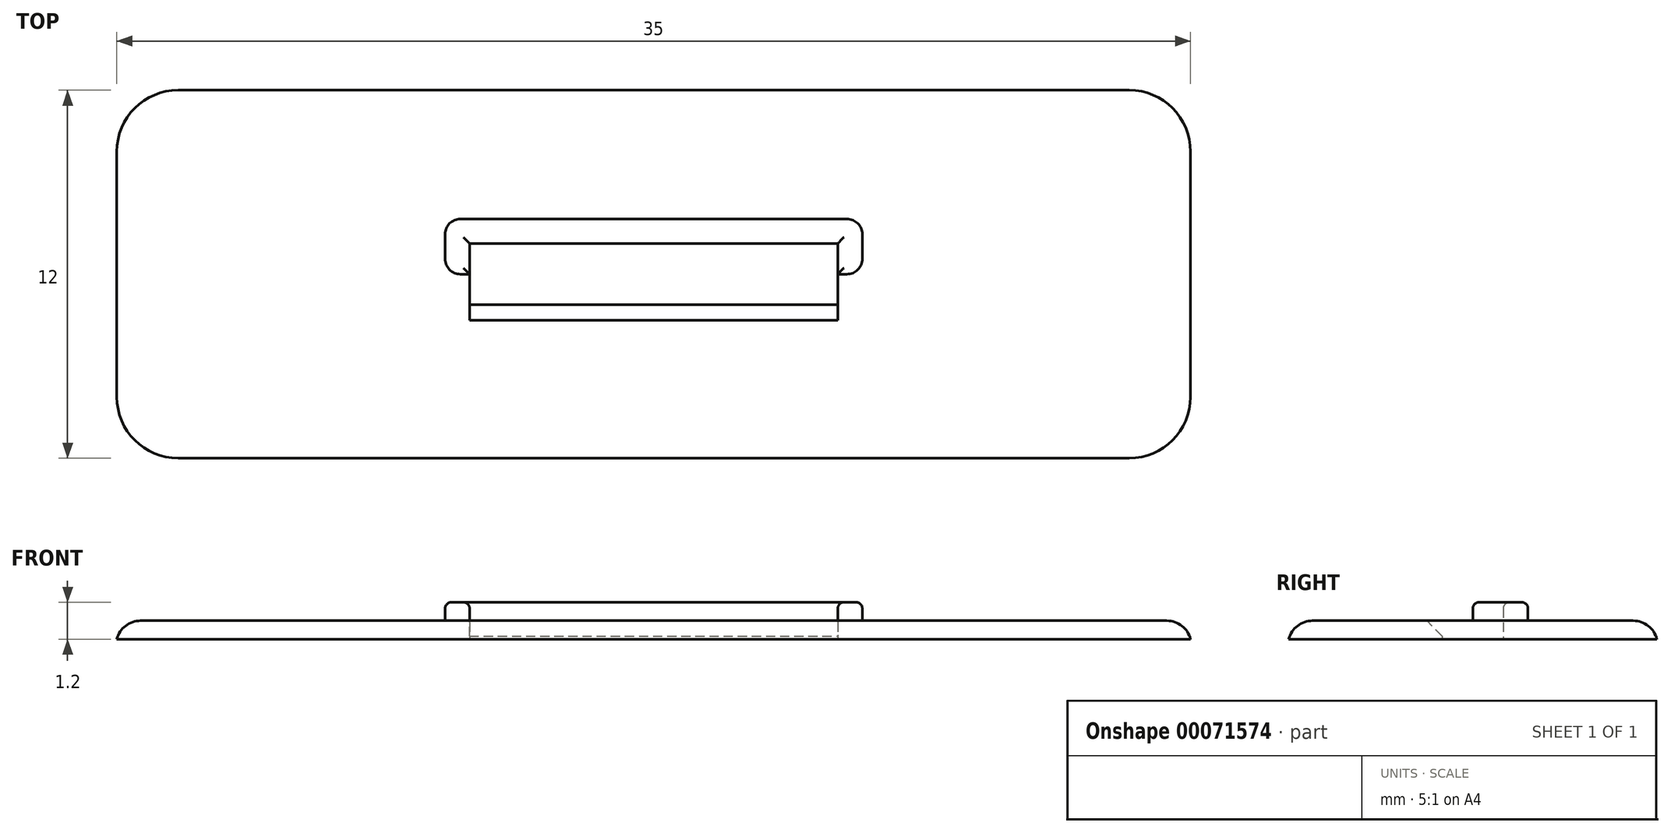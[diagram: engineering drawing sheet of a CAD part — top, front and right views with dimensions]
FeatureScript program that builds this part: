
annotation { "Feature Type Name" : "Feature", "Feature Type Description" : "" }
export const myFeature = defineFeature(function(context is Context, id is Id, definition is map)
    precondition{}
    {
        {
            var Q0;
            Q0=qCreatedBy(makeId("Top.planeOp"),FACE);
            var sketch = newSketch(context, id + "F0", { "sketchPlane" : qUnion([Q0])});
            skLineSegment(sketch, "E0.rect.bottom", {"start": v(17.5, -6) * mm, "end": v(-17.5, -6) * mm});
            skLineSegment(sketch, "E0.rect.top", {"start": v(17.5, 6) * mm, "end": v(-17.5, 6) * mm});
            skLineSegment(sketch, "E0.rect.left", {"start": v(17.5, -6) * mm, "end": v(17.5, 6) * mm});
            skLineSegment(sketch, "E0.rect.right", {"start": v(-17.5, -6) * mm, "end": v(-17.5, 6) * mm});
            skPoint(sketch, "E0.rect.middle", {"position": v(0, 0) * mm});
            skLineSegment(sketch, "E1.bottom", {"start": v(-6, 1) * mm, "end": v(6, 1) * mm});
            skLineSegment(sketch, "E1.top", {"start": v(-6, -1) * mm, "end": v(6, -1) * mm});
            skLineSegment(sketch, "E1.left", {"start": v(-6, 1) * mm, "end": v(-6, -1) * mm});
            skLineSegment(sketch, "E1.right", {"start": v(6, 1) * mm, "end": v(6, -1) * mm});
            skPoint(sketch, "E2", {"position": v(0, 1) * mm});
            skPoint(sketch, "E3", {"position": v(6, 0) * mm});
            skSolve(sketch);
        }
        {
            var Q0;
            Q0=qSketchRegion(id+"F0",true);
            extrude(context, id + "F1", {"entities" : qUnion([Q0]), "depth" : 0.6 * mm});
        }
        {
            var Q0;
            Q0=makeQuery(id+"F1.opExtrude","CAP_FACE",FACE,{"disambiguationData":[OSD([sQuery(id+"F0.wireOp",EDGE,"E0.rect.bottom"),sQuery(id+"F0.wireOp",EDGE,"E0.rect.top"),sQuery(id+"F0.wireOp",EDGE,"E0.rect.left"),sQuery(id+"F0.wireOp",EDGE,"E0.rect.right"),sQuery(id+"F0.wireOp",EDGE,"E1.bottom"),sQuery(id+"F0.wireOp",EDGE,"E1.top"),sQuery(id+"F0.wireOp",EDGE,"E1.left"),sQuery(id+"F0.wireOp",EDGE,"E1.right")])],"isStart":false});
            var sketch = newSketch(context, id + "F2", { "sketchPlane" : qUnion([Q0])});
            skLineSegment(sketch, "E4", {"start": v(-6, 0) * mm, "end": v(-6.8, 0) * mm});
            skPoint(sketch, "E4.endSnap0", {"position": v(-6, 0) * mm});
            skLineSegment(sketch, "E5", {"start": v(-6.8, 0) * mm, "end": v(-6.8, 1.8) * mm});
            skLineSegment(sketch, "E6", {"start": v(-6.8, 1.8) * mm, "end": v(6.8, 1.8) * mm});
            skLineSegment(sketch, "E7", {"start": v(6.8, 1.8) * mm, "end": v(6.8, 0) * mm});
            skLineSegment(sketch, "E8", {"start": v(6.8, 0) * mm, "end": v(6, 0) * mm});
            skSolve(sketch);
        }
        {
            var Q0;
            {var subQ1=sQuery(id+"F2.wireOp",EDGE,"E4");Q0=makeQuery(id+"F2.imprint","IMPRINT",FACE,{"disambiguationData":[TD([[makeQuery(id+"F2.imprint","IMPRINT",EDGE,{"derivedFrom":subQ1}),-1.0]])]});}
            extrude(context, id + "F3", {"entities" : qUnion([Q0]), "operationType" : NewBodyOperationType.ADD, "depth" : 0.6 * mm});
        }
        {
            var Q0;
            Q0=makeQuery(id+"F1.opExtrude","SWEPT_EDGE",EDGE,{"disambiguationData":[OSD([sQuery(id+"F0.wireOp",EDGE,"E0.rect.bottom"),sQuery(id+"F0.wireOp",EDGE,"E0.rect.right")])]});
            var Q1;
            Q1=makeQuery(id+"F1.opExtrude","SWEPT_EDGE",EDGE,{"disambiguationData":[OSD([sQuery(id+"F0.wireOp",EDGE,"E0.rect.top"),sQuery(id+"F0.wireOp",EDGE,"E0.rect.right")])]});
            var Q2;
            Q2=makeQuery(id+"F1.opExtrude","SWEPT_EDGE",EDGE,{"disambiguationData":[OSD([sQuery(id+"F0.wireOp",EDGE,"E0.rect.top"),sQuery(id+"F0.wireOp",EDGE,"E0.rect.left")])]});
            var Q3;
            Q3=makeQuery(id+"F1.opExtrude","SWEPT_EDGE",EDGE,{"disambiguationData":[OSD([sQuery(id+"F0.wireOp",EDGE,"E0.rect.bottom"),sQuery(id+"F0.wireOp",EDGE,"E0.rect.left")])]});
            fillet(context, id + "F4", {"entities" : qUnion([Q0, Q1, Q2, Q3]), "radius" : 2 * mm, "tangentPropagation" : true, "allowEdgeOverflow" : false});
        }
        {
            var Q0;
            Q0=makeQuery(id+"F3.opExtrude","SWEPT_EDGE",EDGE,{"disambiguationData":[OSD([sQuery(id+"F2.wireOp",EDGE,"E6"),sQuery(id+"F2.wireOp",EDGE,"E7")])]});
            var Q1;
            Q1=makeQuery(id+"F3.opExtrude","SWEPT_EDGE",EDGE,{"disambiguationData":[OSD([sQuery(id+"F2.wireOp",EDGE,"E7"),sQuery(id+"F2.wireOp",EDGE,"E8")])]});
            var Q2;
            Q2=makeQuery(id+"F3.opExtrude","SWEPT_EDGE",EDGE,{"disambiguationData":[OSD([sQuery(id+"F2.wireOp",EDGE,"E5"),sQuery(id+"F2.wireOp",EDGE,"E6")])]});
            var Q3;
            Q3=makeQuery(id+"F3.opExtrude","SWEPT_EDGE",EDGE,{"disambiguationData":[OSD([sQuery(id+"F2.wireOp",EDGE,"E4"),sQuery(id+"F2.wireOp",EDGE,"E5")])]});
            fillet(context, id + "F5", {"entities" : qUnion([Q0, Q1, Q2, Q3]), "radius" : 0.5 * mm, "tangentPropagation" : true, "allowEdgeOverflow" : false});
        }
        {
            var Q0;
            Q0=makeQuery(id+"F1.opExtrude","CAP_EDGE",EDGE,{"disambiguationData":[OSD([sQuery(id+"F0.wireOp",EDGE,"E1.top")])],"isStart":false});
            chamfer(context, id + "F6", {"entities" : qUnion([Q0]), "width" : 0.5 * mm, "tangentPropagation" : true});
        }
        {
            var Q0;
            Q0=makeQuery(id+"F1.opExtrude","CAP_EDGE",EDGE,{"disambiguationData":[OSD([sQuery(id+"F0.wireOp",EDGE,"E0.rect.left")])],"isStart":false});
            var Q1;
            {var subQ0=sQuery(id+"F0.wireOp",EDGE,"E0.rect.left");var subQ1=sQuery(id+"F0.wireOp",EDGE,"E0.rect.top");Q1=makeQuery(id+"F4.opFillet","BLEND_EDGE",EDGE,{"blendedFrom":[makeQuery(id+"F1.opExtrude","SWEPT_EDGE",EDGE,{"disambiguationData":[OSD([subQ1,subQ0])]}),makeQuery(id+"F1.opExtrude","CAP_FACE",FACE,{"disambiguationData":[OSD([sQuery(id+"F0.wireOp",EDGE,"E0.rect.bottom"),subQ1,subQ0,sQuery(id+"F0.wireOp",EDGE,"E0.rect.right"),sQuery(id+"F0.wireOp",EDGE,"E1.bottom"),sQuery(id+"F0.wireOp",EDGE,"E1.top"),sQuery(id+"F0.wireOp",EDGE,"E1.left"),sQuery(id+"F0.wireOp",EDGE,"E1.right")])],"isStart":false})],"blendedInto":[makeQuery(id+"F1.opExtrude","CAP_FACE",FACE,{"disambiguationData":[OSD([sQuery(id+"F0.wireOp",EDGE,"E0.rect.bottom"),subQ1,subQ0,sQuery(id+"F0.wireOp",EDGE,"E0.rect.right"),sQuery(id+"F0.wireOp",EDGE,"E1.bottom"),sQuery(id+"F0.wireOp",EDGE,"E1.top"),sQuery(id+"F0.wireOp",EDGE,"E1.left"),sQuery(id+"F0.wireOp",EDGE,"E1.right")])],"isStart":false})]});}
            var Q2;
            Q2=makeQuery(id+"F1.opExtrude","CAP_EDGE",EDGE,{"disambiguationData":[OSD([sQuery(id+"F0.wireOp",EDGE,"E0.rect.top")])],"isStart":false});
            var Q3;
            {var subQ0=sQuery(id+"F0.wireOp",EDGE,"E0.rect.left");var subQ1=sQuery(id+"F0.wireOp",EDGE,"E0.rect.bottom");Q3=makeQuery(id+"F4.opFillet","BLEND_EDGE",EDGE,{"blendedFrom":[makeQuery(id+"F1.opExtrude","SWEPT_EDGE",EDGE,{"disambiguationData":[OSD([subQ1,subQ0])]}),makeQuery(id+"F1.opExtrude","CAP_FACE",FACE,{"disambiguationData":[OSD([subQ1,sQuery(id+"F0.wireOp",EDGE,"E0.rect.top"),subQ0,sQuery(id+"F0.wireOp",EDGE,"E0.rect.right"),sQuery(id+"F0.wireOp",EDGE,"E1.bottom"),sQuery(id+"F0.wireOp",EDGE,"E1.top"),sQuery(id+"F0.wireOp",EDGE,"E1.left"),sQuery(id+"F0.wireOp",EDGE,"E1.right")])],"isStart":false})],"blendedInto":[makeQuery(id+"F1.opExtrude","CAP_FACE",FACE,{"disambiguationData":[OSD([subQ1,sQuery(id+"F0.wireOp",EDGE,"E0.rect.top"),subQ0,sQuery(id+"F0.wireOp",EDGE,"E0.rect.right"),sQuery(id+"F0.wireOp",EDGE,"E1.bottom"),sQuery(id+"F0.wireOp",EDGE,"E1.top"),sQuery(id+"F0.wireOp",EDGE,"E1.left"),sQuery(id+"F0.wireOp",EDGE,"E1.right")])],"isStart":false})]});}
            var Q4;
            Q4=makeQuery(id+"F1.opExtrude","CAP_EDGE",EDGE,{"disambiguationData":[OSD([sQuery(id+"F0.wireOp",EDGE,"E0.rect.bottom")])],"isStart":false});
            var Q5;
            {var subQ0=sQuery(id+"F0.wireOp",EDGE,"E0.rect.right");var subQ1=sQuery(id+"F0.wireOp",EDGE,"E0.rect.bottom");Q5=makeQuery(id+"F4.opFillet","BLEND_EDGE",EDGE,{"blendedFrom":[makeQuery(id+"F1.opExtrude","SWEPT_EDGE",EDGE,{"disambiguationData":[OSD([subQ1,subQ0])]}),makeQuery(id+"F1.opExtrude","CAP_FACE",FACE,{"disambiguationData":[OSD([subQ1,sQuery(id+"F0.wireOp",EDGE,"E0.rect.top"),sQuery(id+"F0.wireOp",EDGE,"E0.rect.left"),subQ0,sQuery(id+"F0.wireOp",EDGE,"E1.bottom"),sQuery(id+"F0.wireOp",EDGE,"E1.top"),sQuery(id+"F0.wireOp",EDGE,"E1.left"),sQuery(id+"F0.wireOp",EDGE,"E1.right")])],"isStart":false})],"blendedInto":[makeQuery(id+"F1.opExtrude","CAP_FACE",FACE,{"disambiguationData":[OSD([subQ1,sQuery(id+"F0.wireOp",EDGE,"E0.rect.top"),sQuery(id+"F0.wireOp",EDGE,"E0.rect.left"),subQ0,sQuery(id+"F0.wireOp",EDGE,"E1.bottom"),sQuery(id+"F0.wireOp",EDGE,"E1.top"),sQuery(id+"F0.wireOp",EDGE,"E1.left"),sQuery(id+"F0.wireOp",EDGE,"E1.right")])],"isStart":false})]});}
            var Q6;
            Q6=makeQuery(id+"F1.opExtrude","CAP_EDGE",EDGE,{"disambiguationData":[OSD([sQuery(id+"F0.wireOp",EDGE,"E0.rect.right")])],"isStart":false});
            var Q7;
            {var subQ0=sQuery(id+"F0.wireOp",EDGE,"E0.rect.right");var subQ1=sQuery(id+"F0.wireOp",EDGE,"E0.rect.top");Q7=makeQuery(id+"F4.opFillet","BLEND_EDGE",EDGE,{"blendedFrom":[makeQuery(id+"F1.opExtrude","SWEPT_EDGE",EDGE,{"disambiguationData":[OSD([subQ1,subQ0])]}),makeQuery(id+"F1.opExtrude","CAP_FACE",FACE,{"disambiguationData":[OSD([sQuery(id+"F0.wireOp",EDGE,"E0.rect.bottom"),subQ1,sQuery(id+"F0.wireOp",EDGE,"E0.rect.left"),subQ0,sQuery(id+"F0.wireOp",EDGE,"E1.bottom"),sQuery(id+"F0.wireOp",EDGE,"E1.top"),sQuery(id+"F0.wireOp",EDGE,"E1.left"),sQuery(id+"F0.wireOp",EDGE,"E1.right")])],"isStart":false})],"blendedInto":[makeQuery(id+"F1.opExtrude","CAP_FACE",FACE,{"disambiguationData":[OSD([sQuery(id+"F0.wireOp",EDGE,"E0.rect.bottom"),subQ1,sQuery(id+"F0.wireOp",EDGE,"E0.rect.left"),subQ0,sQuery(id+"F0.wireOp",EDGE,"E1.bottom"),sQuery(id+"F0.wireOp",EDGE,"E1.top"),sQuery(id+"F0.wireOp",EDGE,"E1.left"),sQuery(id+"F0.wireOp",EDGE,"E1.right")])],"isStart":false})]});}
            fillet(context, id + "F7", {"entities" : qUnion([Q0, Q1, Q2, Q3, Q4, Q5, Q6, Q7]), "radius" : 0.8 * mm, "tangentPropagation" : true, "allowEdgeOverflow" : false});
        }
        {
            var Q0;
            Q0=makeQuery(id+"F3.opExtrude","CAP_EDGE",EDGE,{"disambiguationData":[OSD([sQuery(id+"F2.wireOp",EDGE,"E8")])],"isStart":false});
            var Q1;
            {var subQ0=sQuery(id+"F2.wireOp",EDGE,"E8");var subQ1=sQuery(id+"F2.wireOp",EDGE,"E7");Q1=makeQuery(id+"F5.opFillet","BLEND_EDGE",EDGE,{"blendedFrom":[makeQuery(id+"F3.opExtrude","SWEPT_EDGE",EDGE,{"disambiguationData":[OSD([subQ1,subQ0])]}),makeQuery(id+"F3.opExtrude","CAP_FACE",FACE,{"disambiguationData":[OSD([sQuery(id+"F0.wireOp",EDGE,"E1.bottom"),sQuery(id+"F0.wireOp",EDGE,"E1.left"),sQuery(id+"F0.wireOp",EDGE,"E1.right"),sQuery(id+"F2.wireOp",EDGE,"E4"),sQuery(id+"F2.wireOp",EDGE,"E5"),sQuery(id+"F2.wireOp",EDGE,"E6"),subQ1,subQ0])],"isStart":false})],"blendedInto":[makeQuery(id+"F3.opExtrude","CAP_FACE",FACE,{"disambiguationData":[OSD([sQuery(id+"F0.wireOp",EDGE,"E1.bottom"),sQuery(id+"F0.wireOp",EDGE,"E1.left"),sQuery(id+"F0.wireOp",EDGE,"E1.right"),sQuery(id+"F2.wireOp",EDGE,"E4"),sQuery(id+"F2.wireOp",EDGE,"E5"),sQuery(id+"F2.wireOp",EDGE,"E6"),subQ1,subQ0])],"isStart":false})]});}
            var Q2;
            Q2=makeQuery(id+"F3.opExtrude","CAP_EDGE",EDGE,{"disambiguationData":[OSD([sQuery(id+"F2.wireOp",EDGE,"E7")])],"isStart":false});
            var Q3;
            {var subQ0=sQuery(id+"F2.wireOp",EDGE,"E7");var subQ1=sQuery(id+"F2.wireOp",EDGE,"E6");Q3=makeQuery(id+"F5.opFillet","BLEND_EDGE",EDGE,{"blendedFrom":[makeQuery(id+"F3.opExtrude","SWEPT_EDGE",EDGE,{"disambiguationData":[OSD([subQ1,subQ0])]}),makeQuery(id+"F3.opExtrude","CAP_FACE",FACE,{"disambiguationData":[OSD([sQuery(id+"F0.wireOp",EDGE,"E1.bottom"),sQuery(id+"F0.wireOp",EDGE,"E1.left"),sQuery(id+"F0.wireOp",EDGE,"E1.right"),sQuery(id+"F2.wireOp",EDGE,"E4"),sQuery(id+"F2.wireOp",EDGE,"E5"),subQ1,subQ0,sQuery(id+"F2.wireOp",EDGE,"E8")])],"isStart":false})],"blendedInto":[makeQuery(id+"F3.opExtrude","CAP_FACE",FACE,{"disambiguationData":[OSD([sQuery(id+"F0.wireOp",EDGE,"E1.bottom"),sQuery(id+"F0.wireOp",EDGE,"E1.left"),sQuery(id+"F0.wireOp",EDGE,"E1.right"),sQuery(id+"F2.wireOp",EDGE,"E4"),sQuery(id+"F2.wireOp",EDGE,"E5"),subQ1,subQ0,sQuery(id+"F2.wireOp",EDGE,"E8")])],"isStart":false})]});}
            var Q4;
            Q4=makeQuery(id+"F3.opExtrude","CAP_EDGE",EDGE,{"disambiguationData":[OSD([sQuery(id+"F2.wireOp",EDGE,"E6")])],"isStart":false});
            var Q5;
            {var subQ0=sQuery(id+"F2.wireOp",EDGE,"E6");var subQ1=sQuery(id+"F2.wireOp",EDGE,"E5");Q5=makeQuery(id+"F5.opFillet","BLEND_EDGE",EDGE,{"blendedFrom":[makeQuery(id+"F3.opExtrude","SWEPT_EDGE",EDGE,{"disambiguationData":[OSD([subQ1,subQ0])]}),makeQuery(id+"F3.opExtrude","CAP_FACE",FACE,{"disambiguationData":[OSD([sQuery(id+"F0.wireOp",EDGE,"E1.bottom"),sQuery(id+"F0.wireOp",EDGE,"E1.left"),sQuery(id+"F0.wireOp",EDGE,"E1.right"),sQuery(id+"F2.wireOp",EDGE,"E4"),subQ1,subQ0,sQuery(id+"F2.wireOp",EDGE,"E7"),sQuery(id+"F2.wireOp",EDGE,"E8")])],"isStart":false})],"blendedInto":[makeQuery(id+"F3.opExtrude","CAP_FACE",FACE,{"disambiguationData":[OSD([sQuery(id+"F0.wireOp",EDGE,"E1.bottom"),sQuery(id+"F0.wireOp",EDGE,"E1.left"),sQuery(id+"F0.wireOp",EDGE,"E1.right"),sQuery(id+"F2.wireOp",EDGE,"E4"),subQ1,subQ0,sQuery(id+"F2.wireOp",EDGE,"E7"),sQuery(id+"F2.wireOp",EDGE,"E8")])],"isStart":false})]});}
            var Q6;
            Q6=makeQuery(id+"F3.opExtrude","CAP_EDGE",EDGE,{"disambiguationData":[OSD([sQuery(id+"F2.wireOp",EDGE,"E5")])],"isStart":false});
            var Q7;
            {var subQ0=sQuery(id+"F2.wireOp",EDGE,"E5");var subQ1=sQuery(id+"F2.wireOp",EDGE,"E4");Q7=makeQuery(id+"F5.opFillet","BLEND_EDGE",EDGE,{"blendedFrom":[makeQuery(id+"F3.opExtrude","SWEPT_EDGE",EDGE,{"disambiguationData":[OSD([subQ1,subQ0])]}),makeQuery(id+"F3.opExtrude","CAP_FACE",FACE,{"disambiguationData":[OSD([sQuery(id+"F0.wireOp",EDGE,"E1.bottom"),sQuery(id+"F0.wireOp",EDGE,"E1.left"),sQuery(id+"F0.wireOp",EDGE,"E1.right"),subQ1,subQ0,sQuery(id+"F2.wireOp",EDGE,"E6"),sQuery(id+"F2.wireOp",EDGE,"E7"),sQuery(id+"F2.wireOp",EDGE,"E8")])],"isStart":false})],"blendedInto":[makeQuery(id+"F3.opExtrude","CAP_FACE",FACE,{"disambiguationData":[OSD([sQuery(id+"F0.wireOp",EDGE,"E1.bottom"),sQuery(id+"F0.wireOp",EDGE,"E1.left"),sQuery(id+"F0.wireOp",EDGE,"E1.right"),subQ1,subQ0,sQuery(id+"F2.wireOp",EDGE,"E6"),sQuery(id+"F2.wireOp",EDGE,"E7"),sQuery(id+"F2.wireOp",EDGE,"E8")])],"isStart":false})]});}
            var Q8;
            Q8=makeQuery(id+"F3.opExtrude","CAP_EDGE",EDGE,{"disambiguationData":[OSD([sQuery(id+"F2.wireOp",EDGE,"E4")])],"isStart":false});
            var Q9;
            Q9=makeQuery(id+"F3.opExtrude","CAP_EDGE",EDGE,{"disambiguationData":[OSD([sQuery(id+"F0.wireOp",EDGE,"E1.left")])],"isStart":false});
            var Q10;
            Q10=makeQuery(id+"F3.opExtrude","CAP_EDGE",EDGE,{"disambiguationData":[OSD([sQuery(id+"F0.wireOp",EDGE,"E1.bottom")])],"isStart":false});
            var Q11;
            Q11=makeQuery(id+"F3.opExtrude","CAP_EDGE",EDGE,{"disambiguationData":[OSD([sQuery(id+"F0.wireOp",EDGE,"E1.right")])],"isStart":false});
            fillet(context, id + "F8", {"entities" : qUnion([Q0, Q1, Q2, Q3, Q4, Q5, Q6, Q7, Q8, Q9, Q10, Q11]), "radius" : 0.2 * mm, "tangentPropagation" : true, "allowEdgeOverflow" : false});
        }
    });
